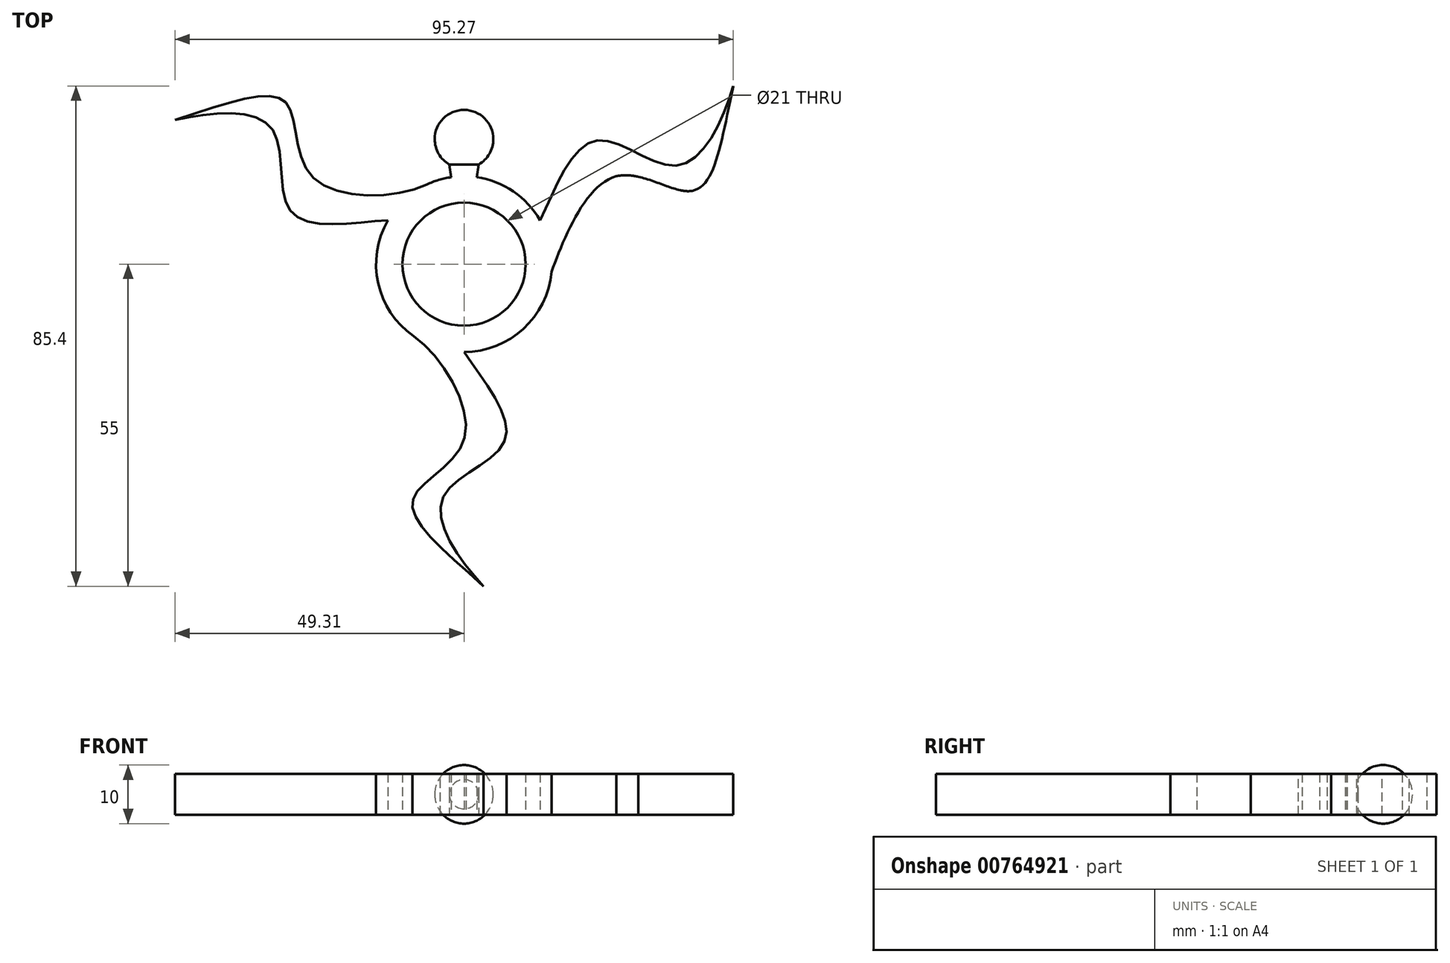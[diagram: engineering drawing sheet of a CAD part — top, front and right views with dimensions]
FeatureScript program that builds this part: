
annotation { "Feature Type Name" : "Feature", "Feature Type Description" : "" }
export const myFeature = defineFeature(function(context is Context, id is Id, definition is map)
    precondition{}
    {
        {
            var Q0;
            Q0=qCreatedBy(makeId("Top.planeOp"),FACE);
            var sketch = newSketch(context, id + "F0", { "sketchPlane" : qUnion([Q0])});
            skCircle(sketch, "E0", {"center": v(0, 0) * mm, "radius": 15 * mm});
            skLineSegment(sketch, "E1", {"start": v(0, 0) * mm, "end": v(0, -58.65) * mm, "construction": true});
            skLineSegment(sketch, "E2", {"start": v(0, 0) * mm, "end": v(37.98, 21.93) * mm, "construction": true});
            skLineSegment(sketch, "E3", {"start": v(0, 0) * mm, "end": v(-36.56, 21.1) * mm, "construction": true});
            skFitSpline(sketch, "E4.MirrorCS", {"points": [v(-6.36, 13.59) * mm, v(-25.98, 15) * mm, v(-30.32, 27.48) * mm, v(-49.3, 24.6) * mm], "startDerivative": vector(-45.6, -21.34) * mm, "endDerivative": vector(-78.42, -25.07) * mm});
            skFitSpline(sketch, "E5.MirrorCS", {"points": [v(-13, 7.5) * mm, v(-29.48, 8.94) * mm, v(-32.82, 23.15) * mm, v(-49.3, 24.6) * mm], "startDerivative": vector(-48.5, -3.02) * mm, "endDerivative": vector(-50.92, -11.46) * mm});
            skFitSpline(sketch, "E6.MirrorCS", {"points": [v(13, 7.5) * mm, v(22.48, 21.06) * mm, v(36.46, 16.85) * mm, v(45.96, 30.4) * mm], "startDerivative": vector(21.64, 43.51) * mm, "endDerivative": vector(15.53, 49.83) * mm});
            skFitSpline(sketch, "E7.MirrorCS", {"points": [v(14.94, -1.29) * mm, v(25.98, 15) * mm, v(38.96, 12.52) * mm, v(45.96, 30.4) * mm], "startDerivative": vector(17.11, 47.34) * mm, "endDerivative": vector(17.5, 80.45) * mm});
            skCircle(sketch, "E8", {"center": v(0, 0) * mm, "radius": 10.5 * mm});
            skPoint(sketch, "E9", {"position": v(6.98, 25.09) * mm});
            skPoint(sketch, "E10.orphan", {"position": v(4.9, 25.73) * mm});
            skPoint(sketch, "E11", {"position": v(2.09, 25.11) * mm});
            skFitSpline(sketch, "E12.MirrorCS", {"points": [v(13, 7.5) * mm, v(22.48, 21.06) * mm, v(36.46, 16.85) * mm, v(45.96, 30.4) * mm], "startDerivative": vector(21.64, 43.51) * mm, "endDerivative": vector(15.53, 49.83) * mm});
            skFitSpline(sketch, "E13.MirrorCS", {"points": [v(14.94, -1.29) * mm, v(25.98, 15) * mm, v(38.96, 12.52) * mm, v(45.96, 30.4) * mm], "startDerivative": vector(4.31, 50.15) * mm, "endDerivative": vector(17.5, 80.45) * mm});
            skLineSegment(sketch, "E14.MirrorCS", {"start": v(0, 0) * mm, "end": v(0, -43.85) * mm, "construction": true});
            skFitSpline(sketch, "E15.MirrorCS", {"points": [v(-6.36, 13.59) * mm, v(-25.98, 15) * mm, v(-30.32, 27.48) * mm, v(-49.3, 24.6) * mm], "startDerivative": vector(-45.6, -21.34) * mm, "endDerivative": vector(-78.42, -25.07) * mm});
            skFitSpline(sketch, "E16.MirrorCS", {"points": [v(-8.59, -12.3) * mm, v(0, -30) * mm, v(-8.64, -40) * mm, v(3.35, -55) * mm], "startDerivative": vector(41.28, -28.81) * mm, "endDerivative": vector(60.92, -55.38) * mm});
            skFitSpline(sketch, "E17.MirrorCS", {"points": [v(0, -15) * mm, v(7, -30) * mm, v(-3.64, -40) * mm, v(3.35, -55) * mm], "startDerivative": vector(26.87, -40.5) * mm, "endDerivative": vector(35.39, -38.37) * mm});
            skPoint(sketch, "E18.1.internal.orphan", {"position": v(-7, -30) * mm});
            skPoint(sketch, "E18.2.internal.orphan", {"position": v(3.64, -40) * mm});
            skPoint(sketch, "E19.0.internal.orphan", {"position": v(8.59, -12.3) * mm});
            skPoint(sketch, "E19.2.internal.orphan", {"position": v(8.64, -40) * mm});
            skPoint(sketch, "E20.orphan", {"position": v(-3.35, -55) * mm});
            skPoint(sketch, "E21.endSnap0", {"position": v(0, -21.93) * mm});
            skSolve(sketch);
        }
        {
            var Q0;
            Q0 = qSketchRegion(id + "F0", true);
            extrude(context, id + "F1", {"entities" : qUnion([Q0]), "endBound" : BoundingType.SYMMETRIC, "depth" : 7 * mm, "offsetDistance" : 25 * mm});
        }
        {
            var Q0;
            Q0=qCreatedBy(makeId("Top.planeOp"),FACE);
            var sketch = newSketch(context, id + "F2", { "sketchPlane" : qUnion([Q0])});
            skLineSegment(sketch, "E22", {"start": v(2.18, 14.84) * mm, "end": v(2.5, 17) * mm});
            skLineSegment(sketch, "E23", {"start": v(-2.18, 14.84) * mm, "end": v(-2.5, 17) * mm});
            skArc(sketch, "E24.0", {"start": v(-2.18, 14.84) * mm, "mid": v(0, 15) * mm, "end": v(2.18, 14.84) * mm});
            skPoint(sketch, "E25.orphan", {"position": v(13, 7.5) * mm});
            skPoint(sketch, "E26.orphan", {"position": v(-6.36, 13.59) * mm});
            skLineSegment(sketch, "E27", {"start": v(-2.5, 17) * mm, "end": v(2.5, 17) * mm});
            skSolve(sketch);
        }
        {
            var Q0;
            Q0=makeQuery(id+"F2.imprint","IMPRINT",FACE,{"disambiguationData":[TD([[makeQuery(id+"F2.imprint","IMPRINT",EDGE,{"derivedFrom":sQuery(id+"F2.wireOp",EDGE,"E22")}),1.0]])]});
            extrude(context, id + "F3", {"entities" : qUnion([Q0]), "operationType" : NewBodyOperationType.ADD, "endBound" : BoundingType.SYMMETRIC, "depth" : 7 * mm, "offsetDistance" : 25 * mm});
        }
        {
            var Q0;
            Q0=qCreatedBy(makeId("Top.planeOp"),FACE);
            var sketch = newSketch(context, id + "F4", { "sketchPlane" : qUnion([Q0])});
            skArc(sketch, "E28", {"start": v(-5, 21.33) * mm, "mid": v(0, 16.33) * mm, "end": v(5, 21.33) * mm});
            skLineSegment(sketch, "E29", {"start": v(-5, 21.33) * mm, "end": v(5, 21.33) * mm});
            skLineSegment(sketch, "E30", {"start": v(-5, 21.33) * mm, "end": v(12.7, 21.33) * mm, "construction": true});
            skSolve(sketch);
        }
        {
            var Q0;
            Q0 = qSketchRegion(id + "F4", true);
            var Q1;
            Q1=sQuery(id+"F4.wireOp",EDGE,"E30");
            revolve(context, id + "F5", {"operationType" : NewBodyOperationType.ADD, "surfaceOperationType" : NewSurfaceOperationType.NEW, "entities" : qUnion([Q0]), "axis" : qUnion([Q1]), "revolveType" : RevolveType.FULL});
        }
    });
